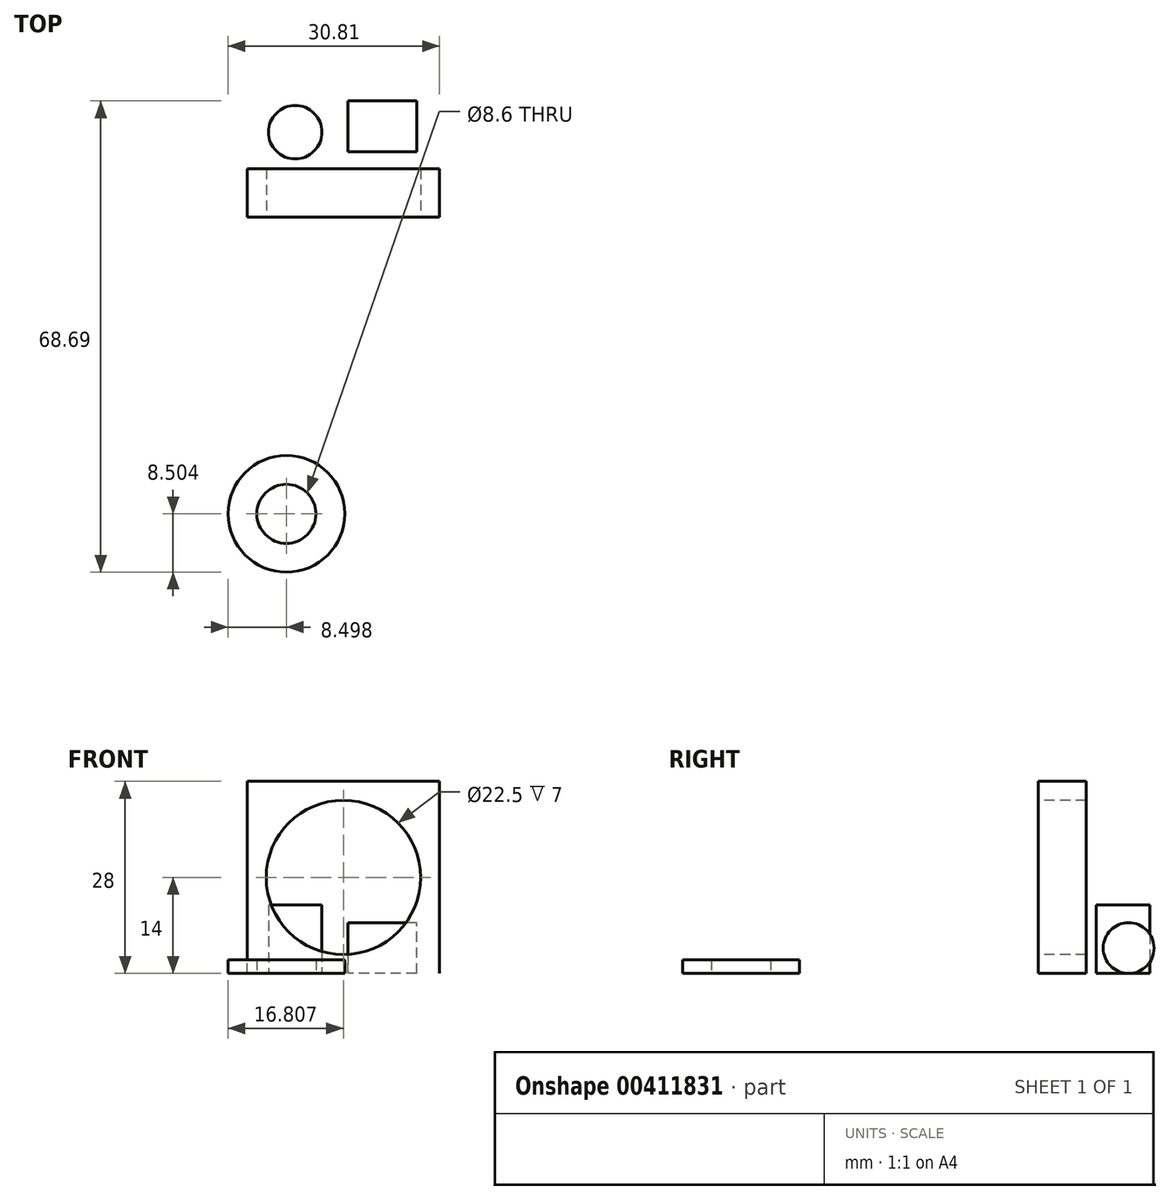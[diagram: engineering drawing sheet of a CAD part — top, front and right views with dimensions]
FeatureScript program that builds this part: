
annotation { "Feature Type Name" : "Feature", "Feature Type Description" : "" }
export const myFeature = defineFeature(function(context is Context, id is Id, definition is map)
    precondition{}
    {
        {
            var Q0;
            Q0=qCreatedBy(makeId("Top.planeOp"),FACE);
            var sketch = newSketch(context, id + "F0", { "sketchPlane" : qUnion([Q0])});
            skCircle(sketch, "E0", {"center": v(-43.7, 12.35) * mm, "radius": 3.9 * mm});
            skSolve(sketch);
        }
        {
            var Q0;
            Q0=makeQuery(id+"F0.imprint","IMPRINT",FACE,{"disambiguationData":[TD([[makeQuery(id+"F0.imprint","IMPRINT",EDGE,{"derivedFrom":sQuery(id+"F0.wireOp",EDGE,"E0")}),1.0]])]});
            extrude(context, id + "F1", {"entities" : qUnion([Q0]), "depth" : 10 * mm});
        }
        {
            var Q0;
            Q0=qCreatedBy(makeId("Right.planeOp"),FACE);
            var sketch = newSketch(context, id + "F2", { "sketchPlane" : qUnion([Q0])});
            skCircle(sketch, "E1", {"center": v(29.2, 3.7) * mm, "radius": 3.7 * mm});
            skPoint(sketch, "E2", {"position": v(29.2, 0) * mm});
            skSolve(sketch);
        }
        {
            var Q0;
            Q0=makeQuery(id+"F2.imprint","IMPRINT",FACE,{"disambiguationData":[TD([[makeQuery(id+"F2.imprint","IMPRINT",EDGE,{"derivedFrom":sQuery(id+"F2.wireOp",EDGE,"E1")}),1.0]])]});
            extrude(context, id + "F3", {"entities" : qUnion([Q0]), "depth" : 10 * mm});
        }
        {
            var Q0;
            Q0=makeQuery(id+"F3.opExtrude","SWEPT_BODY",BODY,{"disambiguationData":[OSD([sQuery(id+"F2.wireOp",EDGE,"E1")])]});
            transform(context, id + "F4", {"entities" : qUnion([Q0]), "transformType" : TransformType.TRANSLATION_3D, "dx" : -36 * mm, "dy" : -16 * mm, "dz" : 0 * mm, "makeCopy" : false});
        }
        {
            var Q0;
            Q0=qCreatedBy(makeId("Front.planeOp"),FACE);
            var sketch = newSketch(context, id + "F5", { "sketchPlane" : qUnion([Q0])});
            skLineSegment(sketch, "E3.bottom", {"start": v(-50.66, 0) * mm, "end": v(-22.66, 0) * mm});
            skLineSegment(sketch, "E3.top", {"start": v(-50.66, 28) * mm, "end": v(-22.66, 28) * mm});
            skLineSegment(sketch, "E3.left", {"start": v(-50.66, 0) * mm, "end": v(-50.66, 28) * mm});
            skLineSegment(sketch, "E3.right", {"start": v(-22.66, 0) * mm, "end": v(-22.66, 28) * mm});
            skPoint(sketch, "E3.middle", {"position": v(-36.66, 14) * mm});
            skCircle(sketch, "E4", {"center": v(-36.66, 14) * mm, "radius": 11.25 * mm});
            skSolve(sketch);
        }
        {
            var Q0;
            Q0=makeQuery(id+"F5.imprint","IMPRINT",FACE,{"disambiguationData":[TD([[makeQuery(id+"F5.imprint","IMPRINT",EDGE,{"derivedFrom":sQuery(id+"F5.wireOp",EDGE,"E3.bottom")}),1.0]])]});
            extrude(context, id + "F6", {"entities" : qUnion([Q0]), "oppositeDirection" : true, "depth" : 7 * mm});
        }
        {
            var Q0;
            Q0=qCreatedBy(makeId("Top.planeOp"),FACE);
            var sketch = newSketch(context, id + "F7", { "sketchPlane" : qUnion([Q0])});
            skCircle(sketch, "E5", {"center": v(-44.97, -43.29) * mm, "radius": 4.3 * mm});
            skCircle(sketch, "E6", {"center": v(-44.97, -43.29) * mm, "radius": 8.5 * mm});
            skSolve(sketch);
        }
        {
            var Q0;
            Q0=makeQuery(id+"F7.imprint","IMPRINT",FACE,{"disambiguationData":[TD([[makeQuery(id+"F7.imprint","IMPRINT",EDGE,{"derivedFrom":sQuery(id+"F7.wireOp",EDGE,"E5")}),-1.0]])]});
            extrude(context, id + "F8", {"entities" : qUnion([Q0]), "depth" : 2 * mm});
        }
    });
